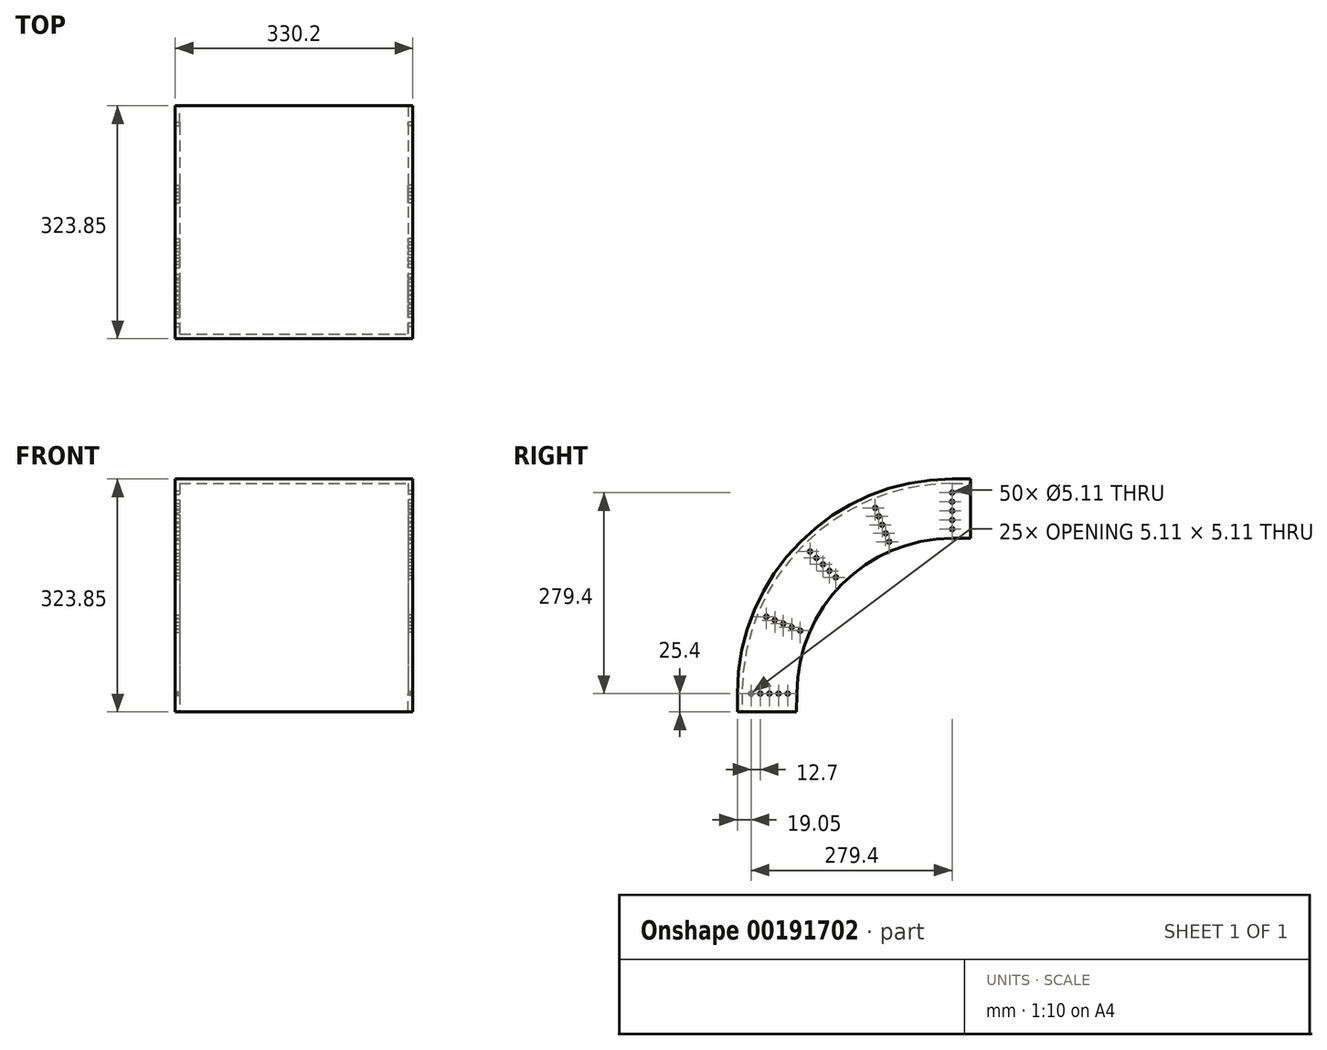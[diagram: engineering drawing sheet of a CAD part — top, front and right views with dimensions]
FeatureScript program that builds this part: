
annotation { "Feature Type Name" : "Feature", "Feature Type Description" : "" }
export const myFeature = defineFeature(function(context is Context, id is Id, definition is map)
    precondition{}
    {
        {
            var Q0;
            Q0=qCreatedBy(makeId("Right.planeOp"),FACE);
            var sketch = newSketch(context, id + "F0", { "sketchPlane" : qUnion([Q0])});
            skLineSegment(sketch, "E0", {"start": v(0, 0) * mm, "end": v(-292.1, 0) * mm, "construction": true});
            skLineSegment(sketch, "E1", {"start": v(0, 0) * mm, "end": v(0, 292.1) * mm, "construction": true});
            skArc(sketch, "E2", {"start": v(0, 292.1) * mm, "mid": v(-206.55, 206.55) * mm, "end": v(-292.1, 0) * mm});
            skArc(sketch, "E3", {"start": v(0, 215.9) * mm, "mid": v(-152.66, 152.66) * mm, "end": v(-215.9, 0) * mm});
            skLineSegment(sketch, "E4", {"start": v(-292.1, 0) * mm, "end": v(-292.1, -25.4) * mm});
            skLineSegment(sketch, "E5", {"start": v(-292.1, -25.4) * mm, "end": v(-216.38, -25.4) * mm});
            skLineSegment(sketch, "E6", {"start": v(-216.38, -25.4) * mm, "end": v(-215.9, 0) * mm});
            skLineSegment(sketch, "E7", {"start": v(0, 292.1) * mm, "end": v(25.4, 292.1) * mm});
            skLineSegment(sketch, "E8", {"start": v(25.4, 292.1) * mm, "end": v(25.4, 215.9) * mm});
            skLineSegment(sketch, "E9", {"start": v(25.4, 215.9) * mm, "end": v(0, 215.9) * mm});
            skSolve(sketch);
        }
        {
            var Q0;
            Q0 = qSketchRegion(id + "F0", true);
            extrude(context, id + "F1", {"entities" : qUnion([Q0]), "depth" : 6.35 * mm});
        }
        {
            var Q0;
            Q0=qCreatedBy(makeId("Right.planeOp"),FACE);
            var sketch = newSketch(context, id + "F2", { "sketchPlane" : qUnion([Q0])});
            skLineSegment(sketch, "E10", {"start": v(0, 0) * mm, "end": v(-254, 0) * mm});
            skCircle(sketch, "E11", {"center": v(-254, 0) * mm, "radius": 2.55 * mm});
            skCircle(sketch, "E12", {"center": v(-241.3, 0) * mm, "radius": 2.55 * mm});
            skCircle(sketch, "E13", {"center": v(-228.6, 0) * mm, "radius": 2.55 * mm});
            skCircle(sketch, "E14", {"center": v(-279.4, 0) * mm, "radius": 2.55 * mm});
            skCircle(sketch, "E15", {"center": v(-266.7, 0) * mm, "radius": 2.55 * mm});
            skCircle(sketch, "E16.1.0", {"center": v(-211.2, 87.48) * mm, "radius": 2.55 * mm});
            skCircle(sketch, "E16.1.1", {"center": v(-222.93, 92.34) * mm, "radius": 2.55 * mm});
            skCircle(sketch, "E16.1.2", {"center": v(-234.67, 97.2) * mm, "radius": 2.55 * mm});
            skCircle(sketch, "E16.1.3", {"center": v(-246.4, 102.06) * mm, "radius": 2.55 * mm});
            skCircle(sketch, "E16.1.4", {"center": v(-258.13, 106.92) * mm, "radius": 2.55 * mm});
            skCircle(sketch, "E16.2.0", {"center": v(-161.64, 161.64) * mm, "radius": 2.55 * mm});
            skCircle(sketch, "E16.2.1", {"center": v(-170.62, 170.62) * mm, "radius": 2.55 * mm});
            skCircle(sketch, "E16.2.2", {"center": v(-179.6, 179.6) * mm, "radius": 2.55 * mm});
            skCircle(sketch, "E16.2.3", {"center": v(-188.59, 188.59) * mm, "radius": 2.55 * mm});
            skCircle(sketch, "E16.2.4", {"center": v(-197.57, 197.57) * mm, "radius": 2.55 * mm});
            skCircle(sketch, "E16.3.0", {"center": v(-87.48, 211.2) * mm, "radius": 2.55 * mm});
            skCircle(sketch, "E16.3.1", {"center": v(-92.34, 222.93) * mm, "radius": 2.55 * mm});
            skCircle(sketch, "E16.3.2", {"center": v(-97.2, 234.67) * mm, "radius": 2.55 * mm});
            skCircle(sketch, "E16.3.3", {"center": v(-102.06, 246.4) * mm, "radius": 2.55 * mm});
            skCircle(sketch, "E16.3.4", {"center": v(-106.92, 258.13) * mm, "radius": 2.55 * mm});
            skCircle(sketch, "E16.4.0", {"center": v(0, 228.6) * mm, "radius": 2.55 * mm});
            skCircle(sketch, "E16.4.1", {"center": v(0, 241.3) * mm, "radius": 2.55 * mm});
            skCircle(sketch, "E16.4.2", {"center": v(0, 254) * mm, "radius": 2.55 * mm});
            skCircle(sketch, "E16.4.3", {"center": v(0, 266.7) * mm, "radius": 2.55 * mm});
            skCircle(sketch, "E16.4.4", {"center": v(0, 279.4) * mm, "radius": 2.55 * mm});
            skPoint(sketch, "E16.center", {"position": v(0, 0) * mm});
            skLineSegment(sketch, "E16.anchor1", {"start": v(0, 0) * mm, "end": v(-279.4, 0) * mm, "construction": true});
            skLineSegment(sketch, "E16.anchor2", {"start": v(0, 0) * mm, "end": v(0, 279.4) * mm, "construction": true});
            skSolve(sketch);
        }
        {
            var Q0;
            Q0=sQuery(id+"F2.wireOp",VERTEX,"E16.2.1.center");
            var Q1;
            Q1=sQuery(id+"F2.wireOp",VERTEX,"E16.1.2.center");
            var Q2;
            Q2=sQuery(id+"F2.wireOp",VERTEX,"E14.center");
            var Q3;
            Q3=sQuery(id+"F2.wireOp",VERTEX,"E16.anchor2.end");
            var Q4;
            Q4=sQuery(id+"F2.wireOp",VERTEX,"E16.4.0.center");
            var Q5;
            Q5=sQuery(id+"F2.wireOp",VERTEX,"E15.center");
            var Q6;
            Q6=sQuery(id+"F2.wireOp",VERTEX,"E16.2.3.center");
            var Q7;
            Q7=sQuery(id+"F2.wireOp",VERTEX,"E16.1.1.center");
            var Q8;
            Q8=sQuery(id+"F2.wireOp",VERTEX,"E16.1.0.center");
            var Q9;
            Q9=sQuery(id+"F2.wireOp",VERTEX,"E16.3.4.center");
            var Q10;
            Q10=sQuery(id+"F2.wireOp",VERTEX,"E11.center");
            var Q11;
            Q11=sQuery(id+"F2.wireOp",VERTEX,"E16.4.3.center");
            var Q12;
            Q12=sQuery(id+"F2.wireOp",VERTEX,"E16.1.3.center");
            var Q13;
            Q13=sQuery(id+"F2.wireOp",VERTEX,"E16.2.4.center");
            var Q14;
            Q14=sQuery(id+"F2.wireOp",VERTEX,"E13.center");
            var Q15;
            Q15=sQuery(id+"F2.wireOp",VERTEX,"E16.1.4.center");
            var Q16;
            Q16=sQuery(id+"F2.wireOp",VERTEX,"E16.3.3.center");
            var Q17;
            Q17=sQuery(id+"F2.wireOp",VERTEX,"E16.3.2.center");
            var Q18;
            Q18=sQuery(id+"F2.wireOp",VERTEX,"E16.2.0.center");
            var Q19;
            Q19=sQuery(id+"F2.wireOp",VERTEX,"E12.center");
            var Q20;
            Q20=sQuery(id+"F2.wireOp",VERTEX,"E16.2.2.center");
            var Q21;
            Q21=sQuery(id+"F2.wireOp",VERTEX,"E16.3.1.center");
            var Q22;
            Q22=sQuery(id+"F2.wireOp",VERTEX,"E16.center");
            var Q23;
            Q23=sQuery(id+"F2.wireOp",VERTEX,"E16.4.2.center");
            var Q24;
            Q24=sQuery(id+"F2.wireOp",VERTEX,"E16.3.0.center");
            var Q25;
            Q25=sQuery(id+"F2.wireOp",VERTEX,"E16.4.1.center");
            var Q26;
            Q26=makeQuery(id+"F1.opExtrude","SWEPT_BODY",BODY,{"disambiguationData":[OSD([sQuery(id+"F0.wireOp",EDGE,"E2"),sQuery(id+"F0.wireOp",EDGE,"E3"),sQuery(id+"F0.wireOp",EDGE,"E4"),sQuery(id+"F0.wireOp",EDGE,"E5"),sQuery(id+"F0.wireOp",EDGE,"E6"),sQuery(id+"F0.wireOp",EDGE,"E7"),sQuery(id+"F0.wireOp",EDGE,"E8"),sQuery(id+"F0.wireOp",EDGE,"E9")])]});
            hole(context, id + "F3", {"style" : HoleStyle.SIMPLE, "endStyle" : HoleEndStyle.THROUGH, "oppositeDirection" : true, "holeDiameter" : 5.1 * mm, "tappedDepth" : 12.7 * mm, "tapClearance" : 3, "locations" : qUnion([Q0, Q1, Q2, Q3, Q4, Q5, Q6, Q7, Q8, Q9, Q10, Q11, Q12, Q13, Q14, Q15, Q16, Q17, Q18, Q19, Q20, Q21, Q22, Q23, Q24, Q25]), "scope" : qUnion([Q26])});
        }
        {
            var Q0;
            Q0=makeQuery(id+"F1.opExtrude","CAP_FACE",FACE,{"disambiguationData":[OSD([sQuery(id+"F0.wireOp",EDGE,"E2"),sQuery(id+"F0.wireOp",EDGE,"E3"),sQuery(id+"F0.wireOp",EDGE,"E4"),sQuery(id+"F0.wireOp",EDGE,"E5"),sQuery(id+"F0.wireOp",EDGE,"E6"),sQuery(id+"F0.wireOp",EDGE,"E7"),sQuery(id+"F0.wireOp",EDGE,"E8"),sQuery(id+"F0.wireOp",EDGE,"E9")])],"isStart":false});
            var sketch = newSketch(context, id + "F4", { "sketchPlane" : qUnion([Q0])});
            skLineSegment(sketch, "E17", {"start": v(-292.1, 0) * mm, "end": v(-292.1, -25.4) * mm});
            skLineSegment(sketch, "E18", {"start": v(-292.1, -25.4) * mm, "end": v(-298.45, -25.4) * mm});
            skLineSegment(sketch, "E19", {"start": v(-298.45, -25.4) * mm, "end": v(-298.45, 0) * mm});
            skLineSegment(sketch, "E20", {"start": v(0, 292.1) * mm, "end": v(25.4, 292.1) * mm});
            skLineSegment(sketch, "E21", {"start": v(25.4, 292.1) * mm, "end": v(25.4, 298.45) * mm});
            skLineSegment(sketch, "E22", {"start": v(25.4, 298.45) * mm, "end": v(0, 298.45) * mm});
            skArc(sketch, "E23", {"start": v(0, 298.45) * mm, "mid": v(-211.04, 211.04) * mm, "end": v(-298.45, 0) * mm});
            skArc(sketch, "E24", {"start": v(0, 292.1) * mm, "mid": v(-206.55, 206.55) * mm, "end": v(-292.1, 0) * mm});
            skSolve(sketch);
        }
        {
            var Q0;
            Q0 = qSketchRegion(id + "F4", true);
            extrude(context, id + "F5", {"entities" : qUnion([Q0]), "operationType" : NewBodyOperationType.ADD, "oppositeDirection" : true, "depth" : 165.1 * mm});
        }
        {
            var Q0;
            Q0=makeQuery(id+"F1.opExtrude","SWEPT_BODY",BODY,{"disambiguationData":[OSD([sQuery(id+"F0.wireOp",EDGE,"E2"),sQuery(id+"F0.wireOp",EDGE,"E3"),sQuery(id+"F0.wireOp",EDGE,"E4"),sQuery(id+"F0.wireOp",EDGE,"E5"),sQuery(id+"F0.wireOp",EDGE,"E6"),sQuery(id+"F0.wireOp",EDGE,"E7"),sQuery(id+"F0.wireOp",EDGE,"E8"),sQuery(id+"F0.wireOp",EDGE,"E9")])]});
            var Q1;
            Q1=makeQuery(id+"F5.opExtrude","CAP_FACE",FACE,{"disambiguationData":[OSD([sQuery(id+"F4.wireOp",EDGE,"E17"),sQuery(id+"F4.wireOp",EDGE,"E18"),sQuery(id+"F4.wireOp",EDGE,"E19"),sQuery(id+"F4.wireOp",EDGE,"E20"),sQuery(id+"F4.wireOp",EDGE,"E21"),sQuery(id+"F4.wireOp",EDGE,"E22"),sQuery(id+"F4.wireOp",EDGE,"E23"),sQuery(id+"F4.wireOp",EDGE,"E24")])],"isStart":false});
            mirror(context, id + "F6", {"operationType" : NewBodyOperationType.ADD, "entities" : qUnion([Q0]), "mirrorPlane" : qUnion([Q1])});
        }
    });
